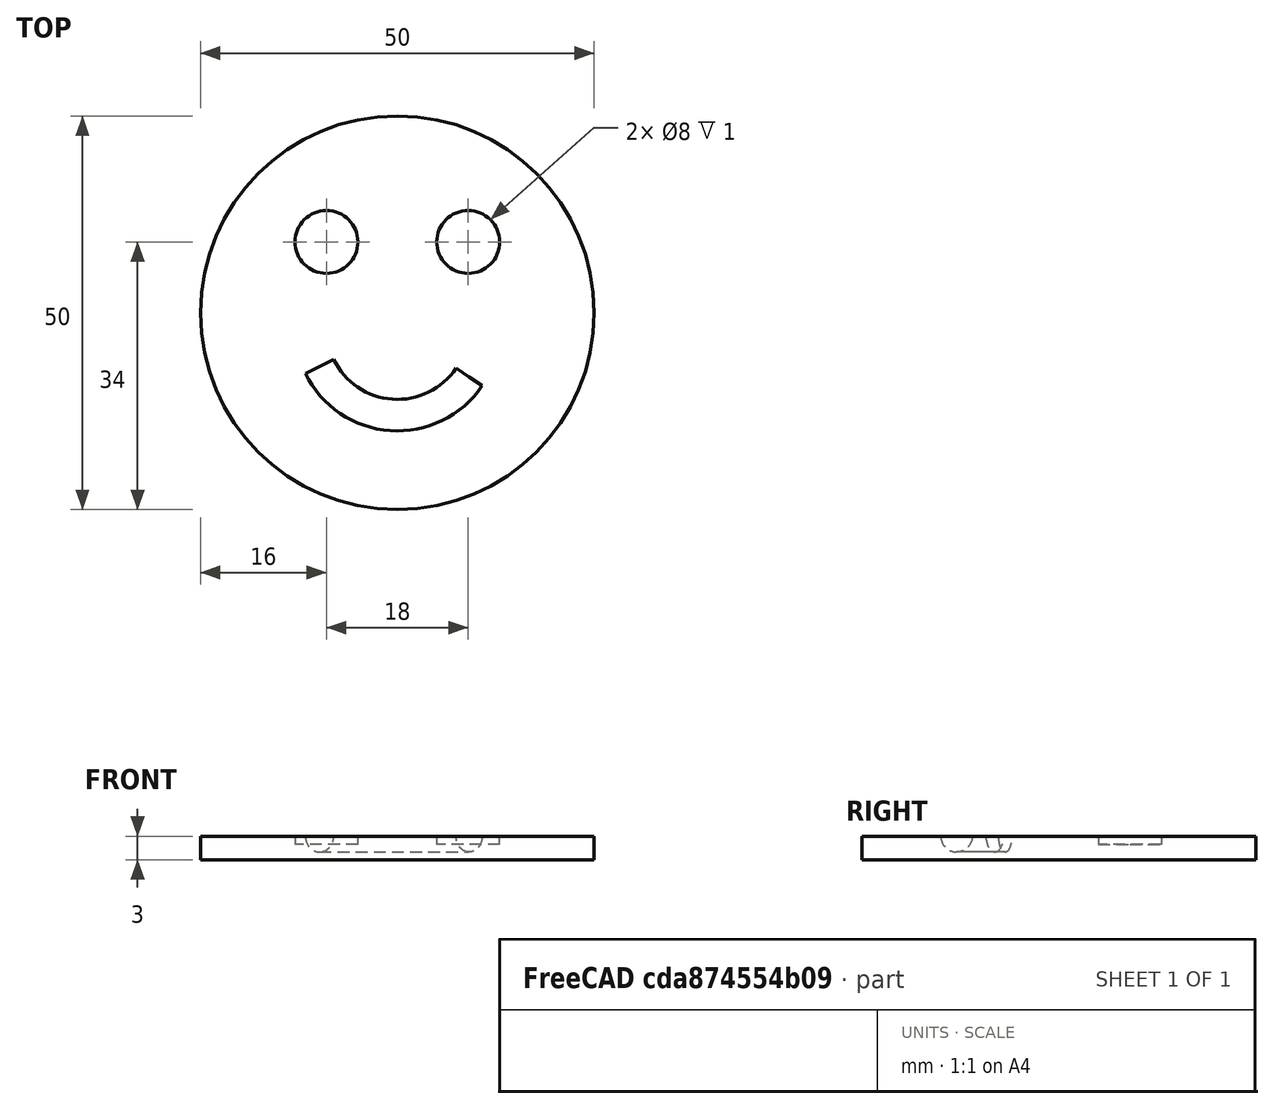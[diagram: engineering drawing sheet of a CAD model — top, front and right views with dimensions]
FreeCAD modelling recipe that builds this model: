
FCSTD DOCUMENT  (FreeCAD 1.0R39319 (Git))
Label: ojt1_t15r01_smile
License: All rights reserved
LicenseURL: https://en.wikipedia.org/wiki/All_rights_reserved
objects: Part::Cylinder×3, Part::Cut×2, Part::Torus×1, Part::MultiFuse×1
note: 7 computed .brp shape members not serialized (recipe doc carries the construction recipe); baked Part::Feature solids carry a one-line shape summary decoded from their .brp

FEATURE [Part::Cylinder] Cylinder  label="Cilindre"
  Angle = 360
  AttacherType = Attacher::AttachEngine3D
  FirstAngle = 0
  Height = 3
  Radius = 25
  SecondAngle = 0
FEATURE [Part::Torus] Torus
  Angle1 = 0
  Angle2 = 180
  Angle3 = 120
  AttacherType = Attacher::AttachEngine3D
  Placement = pos=(0,-2,3) rot=(0,0,1;3.59538rad)
  Radius1 = 11
  Radius2 = 2
FEATURE [Part::Cut] Cut
  Base = -> Cylinder
  Refine = true
  Tool = -> Torus
FEATURE [Part::Cylinder] Cylinder001  label="Cilindre001"
  Angle = 360
  AttacherType = Attacher::AttachEngine3D
  FirstAngle = 0
  Height = 2
  Placement = pos=(-9,9,2) rot=(0,0,1;0rad)
  Radius = 4
  SecondAngle = 0
FEATURE [Part::Cylinder] Cylinder002  label="Cilindre002"
  Angle = 360
  AttacherType = Attacher::AttachEngine3D
  FirstAngle = 0
  Height = 2
  Placement = pos=(9,9,2) rot=(0,0,1;0rad)
  Radius = 4
  SecondAngle = 0
FEATURE [Part::MultiFuse] Fusion
  Refine = true
  Shapes = -> [Cylinder001,Cylinder002]
FEATURE [Part::Cut] Cut001
  Base = -> Cut
  Refine = true
  Tool = -> Fusion
